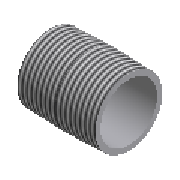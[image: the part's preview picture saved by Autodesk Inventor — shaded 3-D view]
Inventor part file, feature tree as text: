
AUTODESK INVENTOR PART (.ipt)
format: ipt  version: 2023.1 (Build 271208000, 208)  size: 176,640 bytes
history: native  units: mm (DEFAULTED — no unit token found)
features: other x6, revolve x1, sketch x1
ambient origin geometry x8: Origin, YZ Plane, XZ Plane, XY Plane, X Axis, Y Axis, Z Axis, Center Point
bodies: Solid1 (feature_tree)
feature tree (8):
  revolve  "Revolution1"  Angle=90.0deg
  other  "Work Point1"
  other  "Work Axis1"
  other  "Work Point2"
  other  "Work Axis2"
  other  "Work Point3"
  other  "Work Point4"
  sketch  "Sketch1"  dims[d0=52.9mm d12=90.0deg d1=0.312398mm d2=51.0mm d3=0.0mm d4=0.0mm d5=0.0mm d6=0.0mm d7=15.88mm d8=59.614mm]
